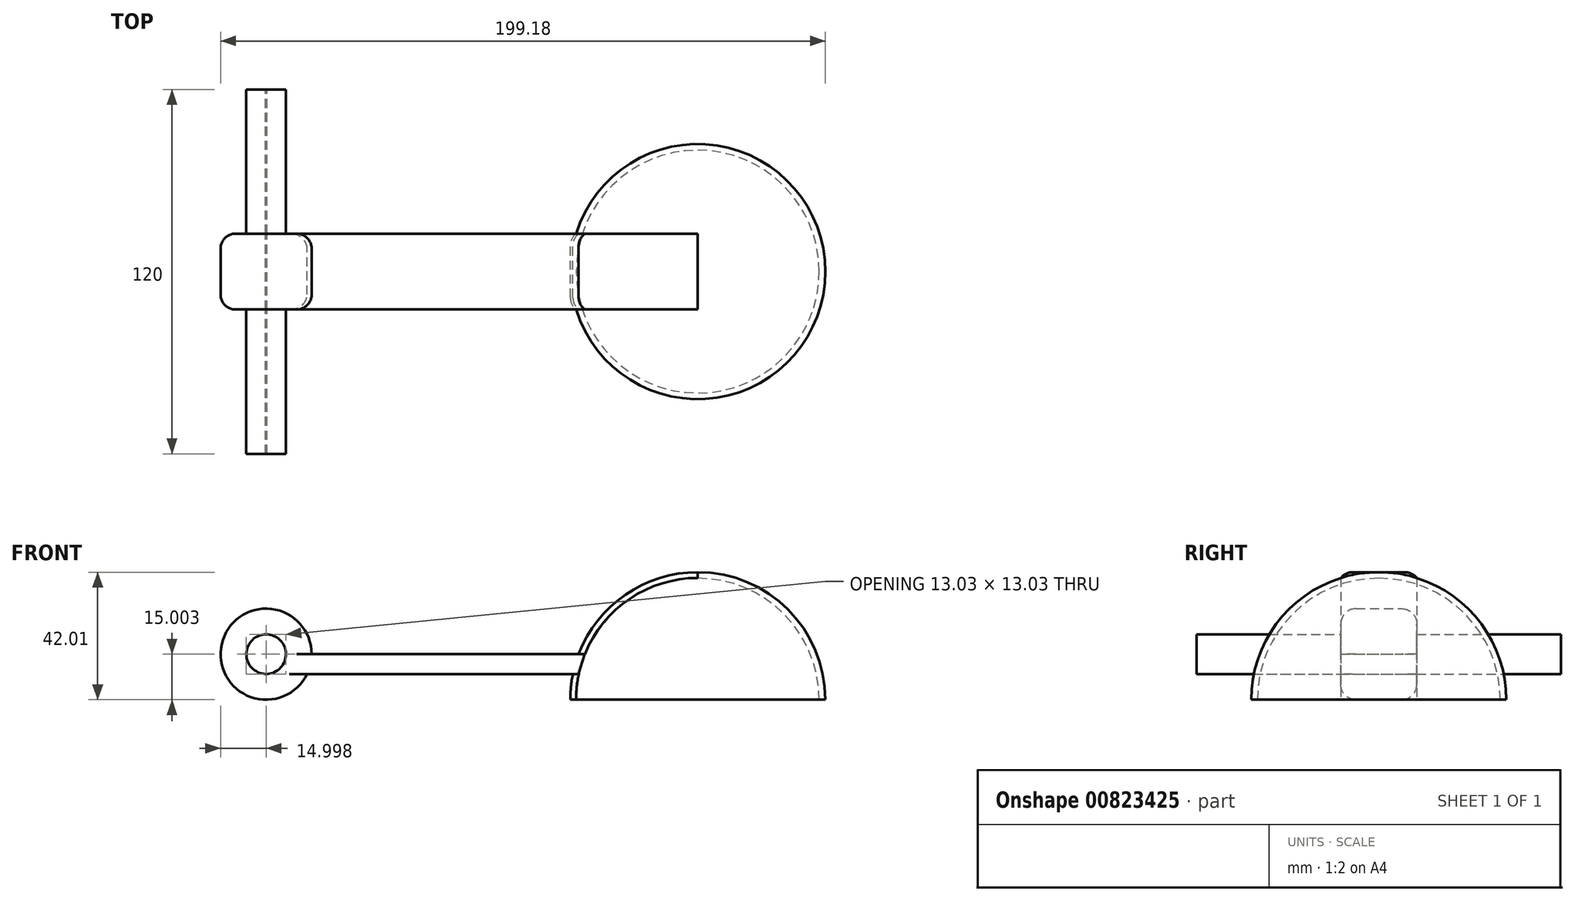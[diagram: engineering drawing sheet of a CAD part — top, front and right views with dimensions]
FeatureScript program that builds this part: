
annotation { "Feature Type Name" : "Feature", "Feature Type Description" : "" }
export const myFeature = defineFeature(function(context is Context, id is Id, definition is map)
    precondition{}
    {
        {
            var Q0;
            Q0=qCreatedBy(makeId("Front.planeOp"),FACE);
            var sketch = newSketch(context, id + "F0", { "sketchPlane" : qUnion([Q0])});
            skLineSegment(sketch, "E0", {"start": v(-42, 0) * mm, "end": v(-40, 0) * mm});
            skLineSegment(sketch, "E1", {"start": v(0, 0) * mm, "end": v(0, 40) * mm});
            skArc(sketch, "E2", {"start": v(-40, 0) * mm, "mid": v(-28.28, 28.28) * mm, "end": v(0, 40) * mm});
            skArc(sketch, "E3.0", {"start": v(-42, 0) * mm, "mid": v(-29.7, 29.7) * mm, "end": v(0, 42) * mm});
            skLineSegment(sketch, "E4", {"start": v(0, 42) * mm, "end": v(0, 40) * mm});
            skPoint(sketch, "E5", {"position": v(0, 20) * mm});
            skPoint(sketch, "E6", {"position": v(-36.93, 20) * mm});
            skPoint(sketch, "E7", {"position": v(-46.93, 20) * mm});
            skArc(sketch, "E8", {"start": v(-36.93, 20) * mm, "mid": v(-36.11, 21.44) * mm, "end": v(-35.24, 22.85) * mm});
            skLineSegment(sketch, "E9", {"start": v(-39.23, 15) * mm, "end": v(-127.18, 15) * mm});
            skCircle(sketch, "E10", {"center": v(-142.18, 15) * mm, "radius": 15 * mm});
            skCircle(sketch, "E11", {"center": v(-142.18, 15) * mm, "radius": 6.52 * mm});
            skLineSegment(sketch, "E12", {"start": v(-142.44, 8.48) * mm, "end": v(-141.92, 8.48) * mm});
            skLineSegment(sketch, "E13.trimOffspring", {"start": v(-128.67, 8.48) * mm, "end": v(-41.13, 8.48) * mm});
            skSolve(sketch);
        }
        {
            var Q0;
            Q0=makeQuery(id+"F0.imprint","IMPRINT",FACE,{"disambiguationData":[TD([[makeQuery(id+"F0.imprint","IMPRINT",EDGE,{"derivedFrom":sQuery(id+"F0.wireOp",EDGE,"E0")}),1.0]])]});
            var Q1;
            Q1=sQuery(id+"F0.wireOp",EDGE,"E1");
            revolve(context, id + "F1", {"entities" : qUnion([Q0]), "axis" : qUnion([Q1]), "revolveType" : RevolveType.FULL, "surfaceOperationType" : NewSurfaceOperationType.NEW});
        }
        {
            var Q0;
            Q0 = qSketchRegion(id + "F0", true);
            extrude(context, id + "F2", {"entities" : qUnion([Q0]), "operationType" : NewBodyOperationType.ADD, "endBound" : BoundingType.SYMMETRIC, "depth" : 25 * mm, "offsetDistance" : 25 * mm});
        }
        {
            var Q0;
            {var subQ0=sQuery(id+"F0.wireOp",EDGE,"E12");Q0=makeQuery(id+"F0.imprint","IMPRINT",FACE,{"disambiguationData":[TD([[makeQuery(id+"F0.imprint","IMPRINT",EDGE,{"derivedFrom":subQ0}),1.0]])]});}
            extrude(context, id + "F3", {"entities" : qUnion([Q0]), "operationType" : NewBodyOperationType.ADD, "endBound" : BoundingType.SYMMETRIC, "depth" : 120 * mm, "offsetDistance" : 25 * mm});
        }
        {
            var Q0;
            Q0=makeQuery(id+"F2.opExtrude","CAP_EDGE",EDGE,{"disambiguationData":[OSD([sQuery(id+"F0.wireOp",EDGE,"E10")])],"isStart":true});
            var Q1;
            Q1=makeQuery(id+"F2.opExtrude","CAP_EDGE",EDGE,{"disambiguationData":[OSD([sQuery(id+"F0.wireOp",EDGE,"E10")])],"isStart":false});
            var Q2;
            Q2=makeQuery(id+"F2.opExtrude","CAP_EDGE",EDGE,{"disambiguationData":[OSD([sQuery(id+"F0.wireOp",EDGE,"E3.0"),sQuery(id+"F0.wireOp",EDGE,"E8")])],"isStart":true});
            var Q3;
            Q3=makeQuery(id+"F2.opExtrude","CAP_EDGE",EDGE,{"disambiguationData":[OSD([sQuery(id+"F0.wireOp",EDGE,"E3.0"),sQuery(id+"F0.wireOp",EDGE,"E8")])],"isStart":false});
            fillet(context, id + "F4", {"entities" : qUnion([Q0, Q1, Q2, Q3]), "radius" : 5 * mm, "tangentPropagation" : true, "allowEdgeOverflow" : false});
        }
    });
